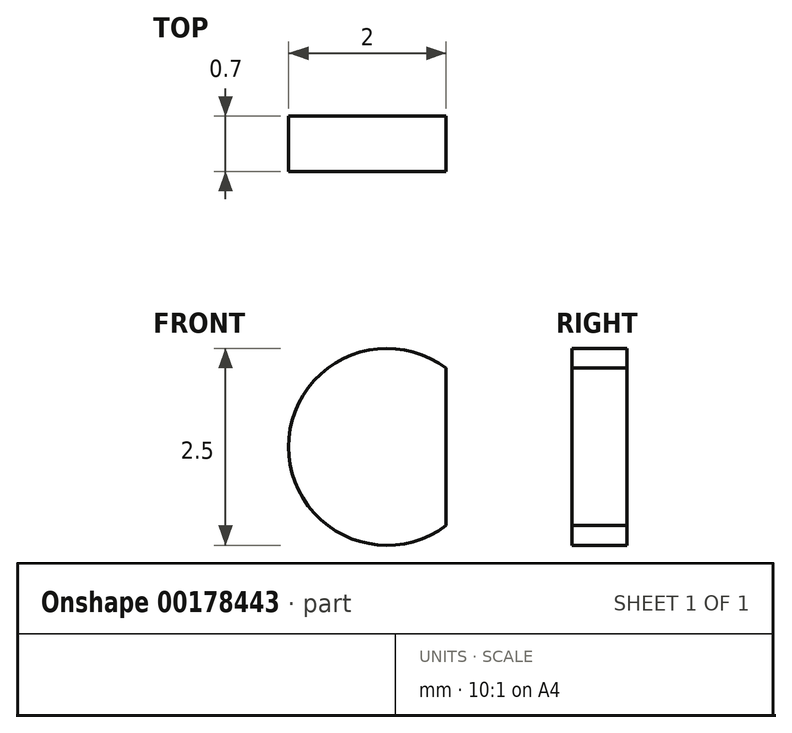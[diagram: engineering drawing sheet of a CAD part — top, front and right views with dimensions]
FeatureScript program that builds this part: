
annotation { "Feature Type Name" : "Feature", "Feature Type Description" : "" }
export const myFeature = defineFeature(function(context is Context, id is Id, definition is map)
    precondition{}
    {
        {
            var Q0;
            Q0=qCreatedBy(makeId("Front.planeOp"),FACE);
            var sketch = newSketch(context, id + "F0", { "sketchPlane" : qUnion([Q0])});
            skArc(sketch, "E0", {"start": v(0.75, 1) * mm, "mid": v(-1.25, 0) * mm, "end": v(0.75, -1) * mm});
            skLineSegment(sketch, "E1", {"start": v(0.75, 1) * mm, "end": v(0.75, -1) * mm});
            skSolve(sketch);
        }
        {
            var Q0;
            Q0 = qSketchRegion(id + "F0", true);
            extrude(context, id + "F1", {"entities" : qUnion([Q0]), "depth" : 0.7 * mm});
        }
    });
